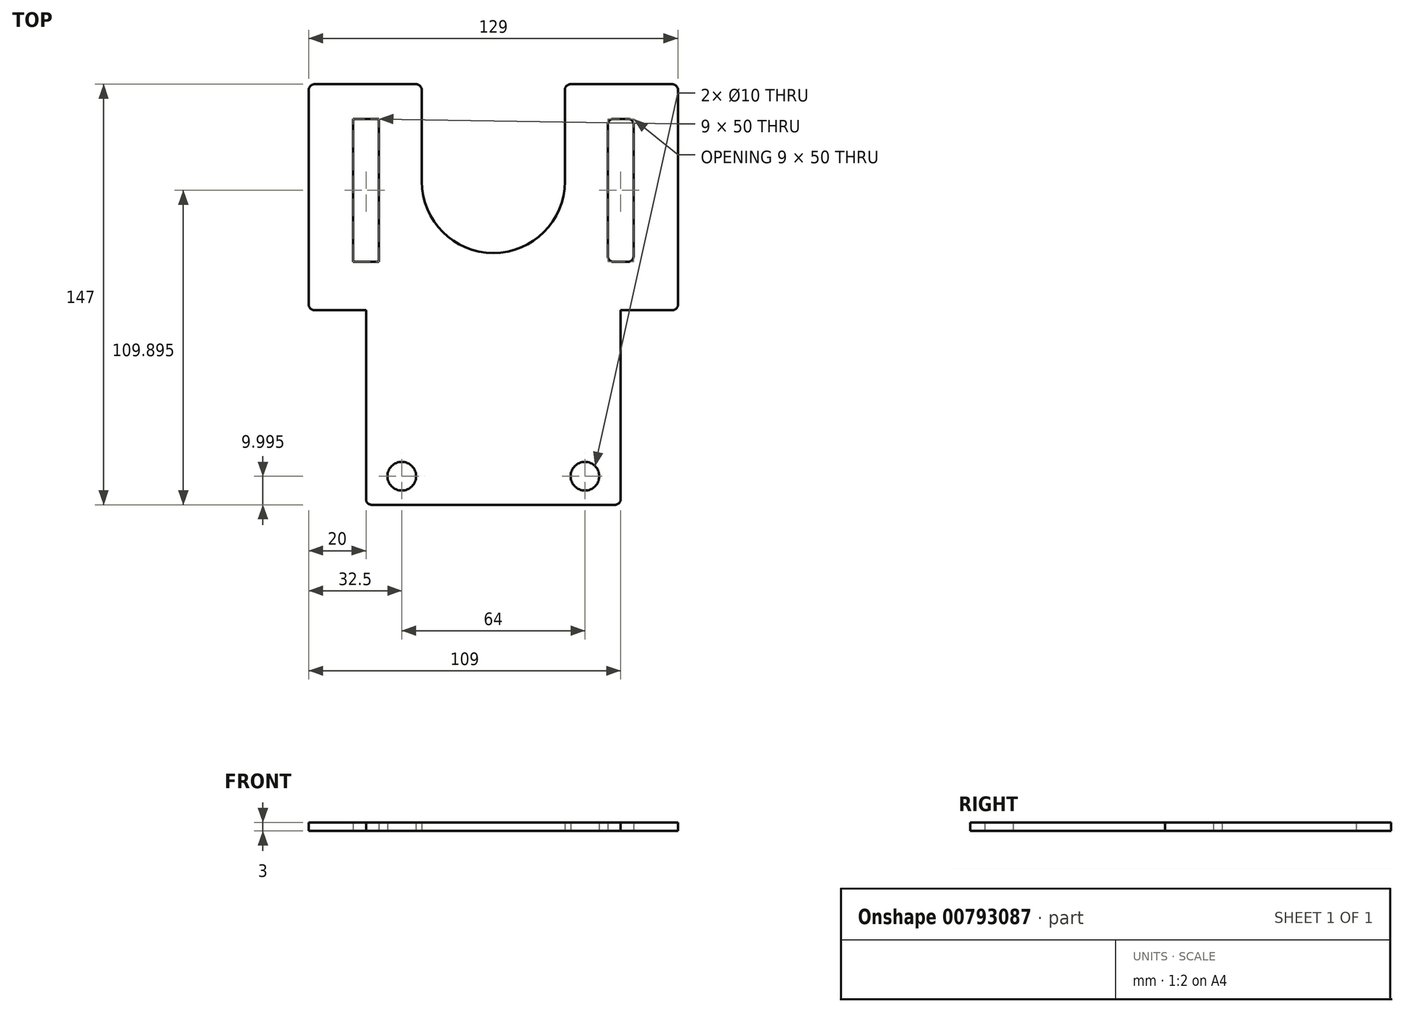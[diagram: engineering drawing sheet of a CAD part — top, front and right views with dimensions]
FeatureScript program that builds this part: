
annotation { "Feature Type Name" : "Feature", "Feature Type Description" : "" }
export const myFeature = defineFeature(function(context is Context, id is Id, definition is map)
    precondition{}
    {
        {
            var Q0;
            Q0=qCreatedBy(makeId("Top.planeOp"),FACE);
            var sketch = newSketch(context, id + "F0", { "sketchPlane" : qUnion([Q0])});
            skLineSegment(sketch, "E0", {"start": v(-140.72, 49.67) * mm, "end": v(-105.22, 49.67) * mm});
            skLineSegment(sketch, "E1", {"start": v(-142.72, 47.67) * mm, "end": v(-142.72, -27.33) * mm});
            skLineSegment(sketch, "E2", {"start": v(-140.72, -29.33) * mm, "end": v(-122.72, -29.33) * mm});
            skLineSegment(sketch, "E3", {"start": v(-122.72, -29.33) * mm, "end": v(-122.72, -95.33) * mm});
            skLineSegment(sketch, "E4", {"start": v(-120.72, -97.33) * mm, "end": v(-35.72, -97.33) * mm});
            skLineSegment(sketch, "E5", {"start": v(-33.72, -95.33) * mm, "end": v(-33.72, -29.33) * mm});
            skLineSegment(sketch, "E6", {"start": v(-33.72, -29.33) * mm, "end": v(-15.72, -29.33) * mm});
            skLineSegment(sketch, "E7", {"start": v(-13.72, -27.33) * mm, "end": v(-13.72, 47.67) * mm});
            skLineSegment(sketch, "E8", {"start": v(-122.72, -29.33) * mm, "end": v(-33.72, -29.33) * mm, "construction": true});
            skLineSegment(sketch, "E9", {"start": v(-78.22, -29.33) * mm, "end": v(-78.22, 15.67) * mm, "construction": true});
            skArc(sketch, "E10", {"start": v(-103.22, 15.67) * mm, "mid": v(-78.22, -9.33) * mm, "end": v(-53.22, 15.67) * mm});
            skLineSegment(sketch, "E11", {"start": v(-78.22, 15.67) * mm, "end": v(-111.67, 15.67) * mm, "construction": true});
            skLineSegment(sketch, "E12", {"start": v(-103.22, 15.67) * mm, "end": v(-103.22, 47.67) * mm});
            skLineSegment(sketch, "E13", {"start": v(-53.22, 47.67) * mm, "end": v(-53.22, 15.67) * mm});
            skLineSegment(sketch, "E14", {"start": v(-33.72, -29.33) * mm, "end": v(-33.72, -12.43) * mm, "construction": true});
            skLineSegment(sketch, "E15", {"start": v(-13.72, 17.46) * mm, "end": v(-29.22, 17.46) * mm, "construction": true});
            skLineSegment(sketch, "E16.bottom", {"start": v(-36.22, 37.57) * mm, "end": v(-31.22, 37.57) * mm});
            skLineSegment(sketch, "E16.top", {"start": v(-36.22, -12.43) * mm, "end": v(-31.22, -12.43) * mm});
            skLineSegment(sketch, "E16.left", {"start": v(-38.22, 35.57) * mm, "end": v(-38.22, -10.43) * mm});
            skLineSegment(sketch, "E16.right", {"start": v(-29.22, 35.57) * mm, "end": v(-29.22, -10.43) * mm});
            skLineSegment(sketch, "E17.MirrorCS", {"start": v(-118.22, 37.57) * mm, "end": v(-118.22, -12.43) * mm});
            skLineSegment(sketch, "E18.MirrorCS", {"start": v(-120.22, 37.57) * mm, "end": v(-125.22, 37.57) * mm});
            skLineSegment(sketch, "E19.MirrorCS", {"start": v(-127.22, 35.57) * mm, "end": v(-127.22, -10.43) * mm});
            skLineSegment(sketch, "E20.MirrorCS", {"start": v(-118.22, -12.43) * mm, "end": v(-127.22, -12.43) * mm});
            skLineSegment(sketch, "E21.MirrorCS", {"start": v(-120.22, -12.43) * mm, "end": v(-125.22, -12.43) * mm});
            skLineSegment(sketch, "E22.MirrorCS", {"start": v(-127.22, 37.57) * mm, "end": v(-127.22, -12.43) * mm});
            skLineSegment(sketch, "E23.MirrorCS", {"start": v(-118.22, 37.57) * mm, "end": v(-127.22, 37.57) * mm});
            skLineSegment(sketch, "E24.MirrorCS", {"start": v(-118.22, 35.57) * mm, "end": v(-118.22, -10.43) * mm});
            skLineSegment(sketch, "E25.trimOffspring", {"start": v(-51.22, 49.67) * mm, "end": v(-15.72, 49.67) * mm});
            skLineSegment(sketch, "E26", {"start": v(-122.72, -97.33) * mm, "end": v(-110.22, -97.33) * mm, "construction": true});
            skLineSegment(sketch, "E27", {"start": v(-110.22, -97.33) * mm, "end": v(-110.22, -87.33) * mm, "construction": true});
            skCircle(sketch, "E28", {"center": v(-110.22, -87.33) * mm, "radius": 5 * mm});
            skLineSegment(sketch, "E29", {"start": v(-110.22, -87.33) * mm, "end": v(-46.22, -87.33) * mm, "construction": true});
            skCircle(sketch, "E30", {"center": v(-46.22, -87.33) * mm, "radius": 5 * mm});
            skPoint(sketch, "E31.visualSharp", {"position": v(-142.72, 49.67) * mm});
            skArc(sketch, "E31.filletArc", {"start": v(-140.72, 49.67) * mm, "mid": v(-142.13, 49.08) * mm, "end": v(-142.72, 47.67) * mm});
            skPoint(sketch, "E32.visualSharp", {"position": v(-142.72, -29.33) * mm});
            skArc(sketch, "E32.filletArc", {"start": v(-142.72, -27.33) * mm, "mid": v(-142.13, -28.75) * mm, "end": v(-140.72, -29.33) * mm});
            skPoint(sketch, "E33.visualSharp", {"position": v(-103.22, 49.67) * mm});
            skArc(sketch, "E33.filletArc", {"start": v(-103.22, 47.67) * mm, "mid": v(-103.8, 49.08) * mm, "end": v(-105.22, 49.67) * mm});
            skPoint(sketch, "E34.visualSharp", {"position": v(-53.22, 49.67) * mm});
            skArc(sketch, "E34.filletArc", {"start": v(-51.22, 49.67) * mm, "mid": v(-52.63, 49.08) * mm, "end": v(-53.22, 47.67) * mm});
            skPoint(sketch, "E35.visualSharp", {"position": v(-13.72, 49.67) * mm});
            skArc(sketch, "E35.filletArc", {"start": v(-13.72, 47.67) * mm, "mid": v(-14.3, 49.08) * mm, "end": v(-15.72, 49.67) * mm});
            skPoint(sketch, "E36.visualSharp", {"position": v(-13.72, -29.33) * mm});
            skArc(sketch, "E36.filletArc", {"start": v(-15.72, -29.33) * mm, "mid": v(-14.3, -28.75) * mm, "end": v(-13.72, -27.33) * mm});
            skPoint(sketch, "E37.visualSharp", {"position": v(-33.72, -97.33) * mm});
            skArc(sketch, "E37.filletArc", {"start": v(-35.72, -97.33) * mm, "mid": v(-34.3, -96.75) * mm, "end": v(-33.72, -95.33) * mm});
            skPoint(sketch, "E38.visualSharp", {"position": v(-122.72, -97.33) * mm});
            skArc(sketch, "E38.filletArc", {"start": v(-122.72, -95.33) * mm, "mid": v(-122.13, -96.75) * mm, "end": v(-120.72, -97.33) * mm});
            skPoint(sketch, "E39.visualSharp", {"position": v(-127.22, 37.57) * mm});
            skArc(sketch, "E39.filletArc", {"start": v(-125.22, 37.57) * mm, "mid": v(-126.63, 36.98) * mm, "end": v(-127.22, 35.57) * mm});
            skPoint(sketch, "E40.visualSharp", {"position": v(-118.22, 37.57) * mm});
            skArc(sketch, "E40.filletArc", {"start": v(-118.22, 35.57) * mm, "mid": v(-118.8, 36.98) * mm, "end": v(-120.22, 37.57) * mm});
            skPoint(sketch, "E41.visualSharp", {"position": v(-118.22, -12.43) * mm});
            skArc(sketch, "E41.filletArc", {"start": v(-120.22, -12.43) * mm, "mid": v(-118.8, -11.85) * mm, "end": v(-118.22, -10.43) * mm});
            skPoint(sketch, "E42.visualSharp", {"position": v(-127.22, -12.43) * mm});
            skArc(sketch, "E42.filletArc", {"start": v(-127.22, -10.43) * mm, "mid": v(-126.63, -11.85) * mm, "end": v(-125.22, -12.43) * mm});
            skPoint(sketch, "E43.visualSharp", {"position": v(-38.22, -12.43) * mm});
            skArc(sketch, "E43.filletArc", {"start": v(-38.22, -10.43) * mm, "mid": v(-37.63, -11.85) * mm, "end": v(-36.22, -12.43) * mm});
            skPoint(sketch, "E44.visualSharp", {"position": v(-29.22, -12.43) * mm});
            skArc(sketch, "E44.filletArc", {"start": v(-31.22, -12.43) * mm, "mid": v(-29.8, -11.85) * mm, "end": v(-29.22, -10.43) * mm});
            skPoint(sketch, "E45.visualSharp", {"position": v(-38.22, 37.57) * mm});
            skArc(sketch, "E45.filletArc", {"start": v(-36.22, 37.57) * mm, "mid": v(-37.63, 36.98) * mm, "end": v(-38.22, 35.57) * mm});
            skPoint(sketch, "E46.visualSharp", {"position": v(-29.22, 37.57) * mm});
            skArc(sketch, "E46.filletArc", {"start": v(-29.22, 35.57) * mm, "mid": v(-29.8, 36.98) * mm, "end": v(-31.22, 37.57) * mm});
            skSolve(sketch);
        }
        {
            var Q0;
            Q0 = qSketchRegion(id + "F0", true);
            extrude(context, id + "F1", {"entities" : qUnion([Q0]), "depth" : 3 * mm, "offsetDistance" : 25 * mm});
        }
    });
